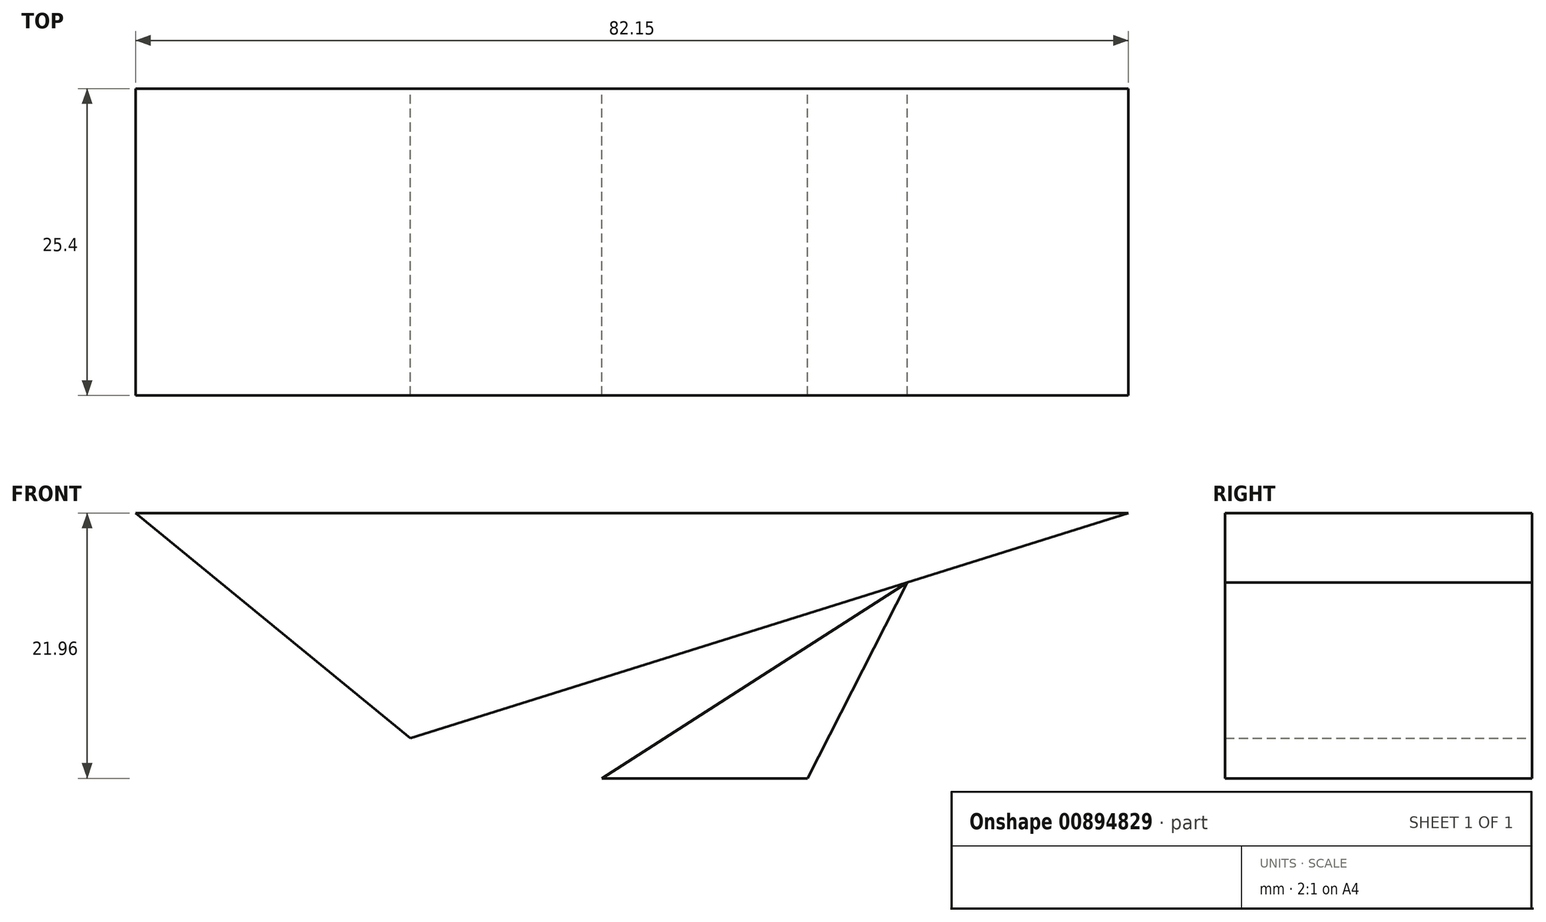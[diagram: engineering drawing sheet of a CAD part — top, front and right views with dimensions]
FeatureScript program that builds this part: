
annotation { "Feature Type Name" : "Feature", "Feature Type Description" : "" }
export const myFeature = defineFeature(function(context is Context, id is Id, definition is map)
    precondition{}
    {
        {
            var Q0;
            Q0=qCreatedBy(makeId("Front.planeOp"),FACE);
            var sketch = newSketch(context, id + "F0", { "sketchPlane" : qUnion([Q0])});
            skLineSegment(sketch, "E0", {"start": v(-34.62, 55.88) * mm, "end": v(47.53, 55.88) * mm});
            skLineSegment(sketch, "E1", {"start": v(47.53, 55.88) * mm, "end": v(-11.88, 37.25) * mm});
            skLineSegment(sketch, "E2", {"start": v(-11.88, 37.25) * mm, "end": v(-34.62, 55.88) * mm});
            skLineSegment(sketch, "E3", {"start": v(21, 33.92) * mm, "end": v(29.25, 50.15) * mm});
            skLineSegment(sketch, "E4", {"start": v(29.25, 50.15) * mm, "end": v(3.96, 33.92) * mm});
            skLineSegment(sketch, "E5", {"start": v(3.96, 33.92) * mm, "end": v(21, 33.92) * mm});
            skSolve(sketch);
        }
        {
            var Q0;
            Q0=makeQuery(id+"F0.imprint","IMPRINT",FACE,{"disambiguationData":[TD([[makeQuery(id+"F0.imprint","IMPRINT",EDGE,{"derivedFrom":sQuery(id+"F0.wireOp",EDGE,"E3")}),1.0]])]});
            var Q1;
            {var subQ0=sQuery(id+"F0.wireOp",EDGE,"E0");Q1=makeQuery(id+"F0.imprint","IMPRINT",FACE,{"disambiguationData":[TD([[makeQuery(id+"F0.imprint","IMPRINT",EDGE,{"derivedFrom":subQ0}),-1.0]])]});}
            extrude(context, id + "F1", {"entities" : qUnion([Q0, Q1]), "depth" : 25.4 * mm, "offsetDistance" : 25.4 * mm});
        }
    });
